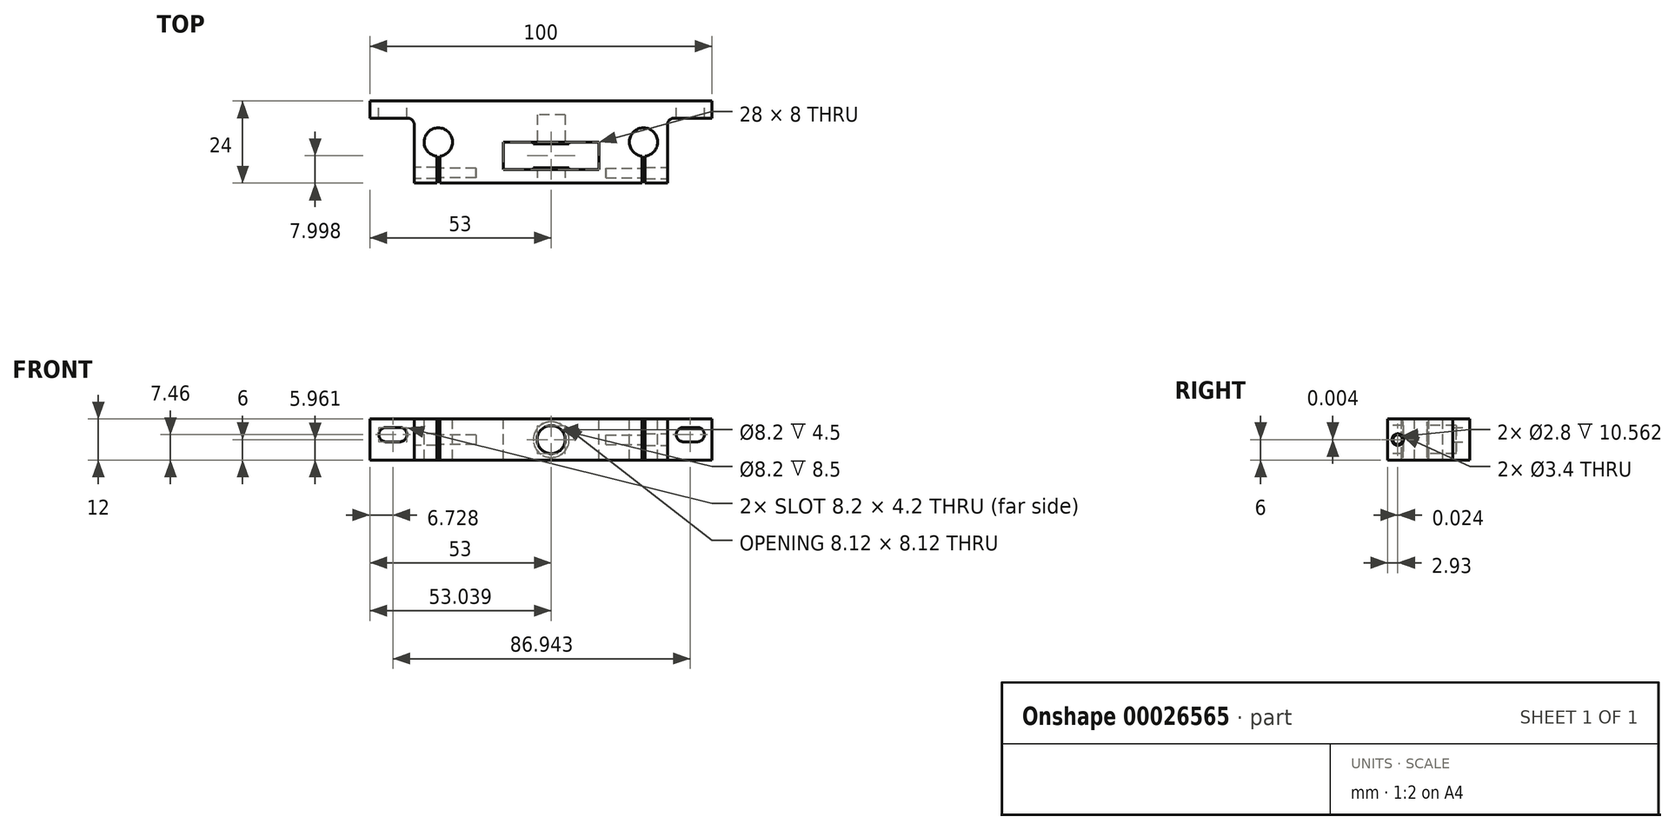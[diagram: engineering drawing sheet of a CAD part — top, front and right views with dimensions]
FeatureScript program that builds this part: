
annotation { "Feature Type Name" : "Feature", "Feature Type Description" : "" }
export const myFeature = defineFeature(function(context is Context, id is Id, definition is map)
    precondition{}
    {
        {
            var Q0;
            Q0=qCreatedBy(makeId("Top.planeOp"),FACE);
            var sketch = newSketch(context, id + "F0", { "sketchPlane" : qUnion([Q0])});
            skLineSegment(sketch, "E0", {"start": v(-46.35, 12.3) * mm, "end": v(53.65, 12.3) * mm});
            skLineSegment(sketch, "E1", {"start": v(53.65, 12.3) * mm, "end": v(53.65, 7.3) * mm});
            skLineSegment(sketch, "E2", {"start": v(53.65, 7.3) * mm, "end": v(40.65, 7.3) * mm});
            skLineSegment(sketch, "E3", {"start": v(40.65, 7.3) * mm, "end": v(40.65, -11.7) * mm});
            skLineSegment(sketch, "E4", {"start": v(40.65, -11.7) * mm, "end": v(-33.35, -11.7) * mm});
            skLineSegment(sketch, "E5", {"start": v(-33.35, -11.7) * mm, "end": v(-33.35, 7.3) * mm});
            skLineSegment(sketch, "E6", {"start": v(-33.35, 7.3) * mm, "end": v(-46.35, 7.3) * mm});
            skLineSegment(sketch, "E7", {"start": v(-46.35, 7.3) * mm, "end": v(-46.35, 12.3) * mm});
            skSolve(sketch);
        }
        {
            var Q0;
            Q0=qSketchRegion(id+"F0",true);
            extrude(context, id + "F1", {"entities" : qUnion([Q0]), "depth" : 12 * mm});
        }
        {
            var Q0;
            Q0=makeQuery(id+"F1.opExtrude","CAP_FACE",FACE,{"disambiguationData":[OSD([sQuery(id+"F0.wireOp",EDGE,"E0"),sQuery(id+"F0.wireOp",EDGE,"E1"),sQuery(id+"F0.wireOp",EDGE,"E2"),sQuery(id+"F0.wireOp",EDGE,"E3"),sQuery(id+"F0.wireOp",EDGE,"E4"),sQuery(id+"F0.wireOp",EDGE,"E5"),sQuery(id+"F0.wireOp",EDGE,"E6"),sQuery(id+"F0.wireOp",EDGE,"E7")])],"isStart":false});
            var sketch = newSketch(context, id + "F2", { "sketchPlane" : qUnion([Q0])});
            skCircle(sketch, "E8", {"center": v(-26.35, 0.3) * mm, "radius": 4.15 * mm});
            skCircle(sketch, "E9", {"center": v(33.65, 0.3) * mm, "radius": 4.15 * mm});
            skPoint(sketch, "E10", {"position": v(3.65, 12.3) * mm});
            skLineSegment(sketch, "E11.bottom", {"start": v(33.21, -3.01) * mm, "end": v(34.09, -3.01) * mm});
            skLineSegment(sketch, "E11.top", {"start": v(33.21, -12.27) * mm, "end": v(34.09, -12.27) * mm});
            skLineSegment(sketch, "E11.left", {"start": v(33.21, -3.01) * mm, "end": v(33.21, -12.27) * mm});
            skLineSegment(sketch, "E11.right", {"start": v(34.09, -3.01) * mm, "end": v(34.09, -12.27) * mm});
            skPoint(sketch, "E12", {"position": v(33.65, -3.01) * mm});
            skLineSegment(sketch, "E13", {"start": v(3.65, 12.3) * mm, "end": v(3.65, -11.7) * mm, "construction": true});
            skLineSegment(sketch, "E14.MirrorCS", {"start": v(-25.91, -12.27) * mm, "end": v(-26.79, -12.27) * mm});
            skLineSegment(sketch, "E15.MirrorCS", {"start": v(-26.79, -3.01) * mm, "end": v(-26.79, -12.27) * mm});
            skLineSegment(sketch, "E16.MirrorCS", {"start": v(-25.91, -3.01) * mm, "end": v(-26.79, -3.01) * mm});
            skLineSegment(sketch, "E17.MirrorCS", {"start": v(-25.91, -3.01) * mm, "end": v(-25.91, -12.27) * mm});
            skSolve(sketch);
        }
        {
            var Q0;
            Q0=qSketchRegion(id+"F2",true);
            var Q1;
            {var subQ3=sQuery(id+"F2.wireOp",EDGE,"E11.bottom");Q1=makeQuery(id+"F2.imprint","IMPRINT",FACE,{"disambiguationData":[TD([[makeQuery(id+"F2.imprint","IMPRINT",EDGE,{"derivedFrom":subQ3}),-1.0]])]});}
            var Q2;
            {var subQ3=sQuery(id+"F2.wireOp",EDGE,"E16.MirrorCS");Q2=makeQuery(id+"F2.imprint","IMPRINT",FACE,{"disambiguationData":[TD([[makeQuery(id+"F2.imprint","IMPRINT",EDGE,{"derivedFrom":subQ3}),1.0]])]});}
            extrude(context, id + "F3", {"entities" : qUnion([Q0, Q1, Q2]), "operationType" : NewBodyOperationType.REMOVE, "endBound" : BoundingType.THROUGH_ALL, "oppositeDirection" : true, "depth" : 25 * mm});
        }
        {
            var Q0;
            Q0=makeQuery(id+"F1.opExtrude","SWEPT_FACE",FACE,{"disambiguationData":[OSD([sQuery(id+"F0.wireOp",EDGE,"E0")])]});
            var sketch = newSketch(context, id + "F4", { "sketchPlane" : qUnion([Q0])});
            skLineSegment(sketch, "E18", {"start": v(-53.65, 7.46) * mm, "end": v(46.35, 7.46) * mm, "construction": true});
            skLineSegment(sketch, "E19.bottom", {"start": v(-49.32, 9.56) * mm, "end": v(-45.32, 9.56) * mm});
            skLineSegment(sketch, "E19.top", {"start": v(-49.32, 5.36) * mm, "end": v(-45.32, 5.36) * mm});
            skArc(sketch, "E20", {"start": v(-45.32, 5.36) * mm, "mid": v(-43.22, 7.46) * mm, "end": v(-45.32, 9.56) * mm});
            skArc(sketch, "E21", {"start": v(-49.32, 9.56) * mm, "mid": v(-51.42, 7.46) * mm, "end": v(-49.32, 5.36) * mm});
            skLineSegment(sketch, "E22.top", {"start": v(37.62, 5.36) * mm, "end": v(41.62, 5.36) * mm});
            skLineSegment(sketch, "E22.bottom", {"start": v(37.62, 9.56) * mm, "end": v(41.62, 9.56) * mm});
            skArc(sketch, "E23", {"start": v(37.62, 9.56) * mm, "mid": v(35.52, 7.46) * mm, "end": v(37.62, 5.36) * mm});
            skArc(sketch, "E24", {"start": v(41.62, 5.36) * mm, "mid": v(43.72, 7.46) * mm, "end": v(41.62, 9.56) * mm});
            skSolve(sketch);
        }
        {
            var Q0;
            Q0=qSketchRegion(id+"F4",true);
            extrude(context, id + "F5", {"entities" : qUnion([Q0]), "operationType" : NewBodyOperationType.REMOVE, "endBound" : BoundingType.THROUGH_ALL, "oppositeDirection" : true, "depth" : 25 * mm});
        }
        {
            var Q0;
            Q0=makeQuery(id+"F1.opExtrude","SWEPT_FACE",FACE,{"disambiguationData":[OSD([sQuery(id+"F0.wireOp",EDGE,"E4")])]});
            var sketch = newSketch(context, id + "F6", { "sketchPlane" : qUnion([Q0])});
            skLineSegment(sketch, "E25", {"start": v(-33.35, 6) * mm, "end": v(40.65, 6) * mm, "construction": true});
            skCircle(sketch, "E26", {"center": v(6.65, 6) * mm, "radius": 4.1 * mm});
            skSolve(sketch);
        }
        {
            var Q0;
            Q0=qSketchRegion(id+"F6",true);
            extrude(context, id + "F7", {"entities" : qUnion([Q0]), "operationType" : NewBodyOperationType.REMOVE, "oppositeDirection" : true, "depth" : 20 * mm});
        }
        {
            var Q0;
            Q0=makeQuery(id+"F1.opExtrude","CAP_FACE",FACE,{"disambiguationData":[OSD([sQuery(id+"F0.wireOp",EDGE,"E0"),sQuery(id+"F0.wireOp",EDGE,"E1"),sQuery(id+"F0.wireOp",EDGE,"E2"),sQuery(id+"F0.wireOp",EDGE,"E3"),sQuery(id+"F0.wireOp",EDGE,"E4"),sQuery(id+"F0.wireOp",EDGE,"E5"),sQuery(id+"F0.wireOp",EDGE,"E6"),sQuery(id+"F0.wireOp",EDGE,"E7")])],"isStart":false});
            var sketch = newSketch(context, id + "F8", { "sketchPlane" : qUnion([Q0])});
            skLineSegment(sketch, "E27.bottom", {"start": v(-7.35, 0.3) * mm, "end": v(20.65, 0.3) * mm});
            skLineSegment(sketch, "E27.top", {"start": v(-7.35, -7.7) * mm, "end": v(20.65, -7.7) * mm});
            skLineSegment(sketch, "E27.left", {"start": v(-7.35, 0.3) * mm, "end": v(-7.35, -7.7) * mm});
            skLineSegment(sketch, "E27.right", {"start": v(20.65, 0.3) * mm, "end": v(20.65, -7.7) * mm});
            skLineSegment(sketch, "E28", {"start": v(6.65, 12.3) * mm, "end": v(6.65, -11.7) * mm, "construction": true});
            skLineSegment(sketch, "E29", {"start": v(6.65, 0.3) * mm, "end": v(6.65, -7.7) * mm});
            skSolve(sketch);
        }
        {
            var Q0;
            Q0=qSketchRegion(id+"F8",true);
            extrude(context, id + "F9", {"entities" : qUnion([Q0]), "operationType" : NewBodyOperationType.REMOVE, "endBound" : BoundingType.THROUGH_ALL, "oppositeDirection" : true, "depth" : 25 * mm});
        }
        {
            var Q0;
            Q0=makeQuery(id+"F9.boolean.opBoolean","COPY",FACE,{"derivedFrom":makeQuery(id+"F9.opExtrude","SWEPT_FACE",FACE,{"disambiguationData":[OSD([sQuery(id+"F8.wireOp",EDGE,"E27.bottom")])]})});
            var sketch = newSketch(context, id + "F10", { "sketchPlane" : qUnion([Q0])});
            skCircle(sketch, "E30", {"center": v(6.65, 6) * mm, "radius": 5.2 * mm});
            skSolve(sketch);
        }
        {
            var Q0;
            Q0=makeQuery(id+"F10.imprint","IMPRINT",FACE,{"disambiguationData":[TD([[makeQuery(id+"F10.imprint","IMPRINT",EDGE,{"derivedFrom":sQuery(id+"F10.wireOp",EDGE,"E30")}),1.0]])]});
            extrude(context, id + "F11", {"entities" : qUnion([Q0]), "operationType" : NewBodyOperationType.ADD, "depth" : 0.5 * mm});
        }
        {
            var Q0;
            Q0=makeQuery(id+"F9.boolean.opBoolean","COPY",FACE,{"derivedFrom":makeQuery(id+"F9.opExtrude","SWEPT_FACE",FACE,{"disambiguationData":[OSD([sQuery(id+"F8.wireOp",EDGE,"E27.top")])]})});
            var sketch = newSketch(context, id + "F12", { "sketchPlane" : qUnion([Q0])});
            skCircle(sketch, "E31", {"center": v(-6.65, 6) * mm, "radius": 5.25 * mm});
            skSolve(sketch);
        }
        {
            var Q0;
            Q0=makeQuery(id+"F12.imprint","IMPRINT",FACE,{"disambiguationData":[TD([[makeQuery(id+"F12.imprint","IMPRINT",EDGE,{"derivedFrom":sQuery(id+"F12.wireOp",EDGE,"E31")}),1.0]])]});
            extrude(context, id + "F13", {"entities" : qUnion([Q0]), "operationType" : NewBodyOperationType.ADD, "depth" : 0.5 * mm});
        }
        {
            var Q0;
            Q0=makeQuery(id+"F1.opExtrude","SWEPT_FACE",FACE,{"disambiguationData":[OSD([sQuery(id+"F0.wireOp",EDGE,"E3")])]});
            var sketch = newSketch(context, id + "F14", { "sketchPlane" : qUnion([Q0])});
            skCircle(sketch, "E32", {"center": v(-8.74, 6) * mm, "radius": 1.7 * mm});
            skCircle(sketch, "E33", {"center": v(-8.74, 6) * mm, "radius": 1.4 * mm});
            skLineSegment(sketch, "E34", {"start": v(-11.7, 6) * mm, "end": v(-3.84, 6) * mm, "construction": true});
            skSolve(sketch);
        }
        {
            var Q0;
            Q0=makeQuery(id+"F14.imprint","IMPRINT",FACE,{"disambiguationData":[TD([[makeQuery(id+"F14.imprint","IMPRINT",EDGE,{"derivedFrom":sQuery(id+"F14.wireOp",EDGE,"E33")}),1.0]])]});
            extrude(context, id + "F15", {"entities" : qUnion([Q0]), "operationType" : NewBodyOperationType.REMOVE, "oppositeDirection" : true, "depth" : 18 * mm});
        }
        {
            var Q0;
            Q0=makeQuery(id+"F14.imprint","IMPRINT",FACE,{"disambiguationData":[TD([[makeQuery(id+"F14.imprint","IMPRINT",EDGE,{"derivedFrom":sQuery(id+"F14.wireOp",EDGE,"E33")}),1.0]])]});
            var Q1;
            Q1=makeQuery(id+"F14.imprint","IMPRINT",FACE,{"disambiguationData":[TD([[makeQuery(id+"F14.imprint","IMPRINT",EDGE,{"derivedFrom":sQuery(id+"F14.wireOp",EDGE,"E32")}),1.0]])]});
            extrude(context, id + "F16", {"entities" : qUnion([Q0, Q1]), "operationType" : NewBodyOperationType.REMOVE, "endBound" : BoundingType.UP_TO_NEXT, "oppositeDirection" : true, "depth" : 7 * mm});
        }
        {
            var Q0;
            Q0=makeQuery(id+"F1.opExtrude","SWEPT_EDGE",EDGE,{"disambiguationData":[OSD([sQuery(id+"F0.wireOp",EDGE,"E2"),sQuery(id+"F0.wireOp",EDGE,"E3")])]});
            fillet(context, id + "F17", {"entities" : qUnion([Q0]), "radius" : 2 * mm, "tangentPropagation" : true, "allowEdgeOverflow" : false});
        }
        {
            var Q0;
            Q0=makeQuery(id+"F1.opExtrude","SWEPT_FACE",FACE,{"disambiguationData":[OSD([sQuery(id+"F0.wireOp",EDGE,"E5")])]});
            var sketch = newSketch(context, id + "F18", { "sketchPlane" : qUnion([Q0])});
            skCircle(sketch, "E35", {"center": v(8.76, 6) * mm, "radius": 1.7 * mm});
            skCircle(sketch, "E36", {"center": v(8.76, 6) * mm, "radius": 1.4 * mm});
            skLineSegment(sketch, "E37", {"start": v(8.76, 0) * mm, "end": v(8.76, 12) * mm, "construction": true});
            skSolve(sketch);
        }
        {
            var Q0;
            Q0=makeQuery(id+"F18.imprint","IMPRINT",FACE,{"disambiguationData":[TD([[makeQuery(id+"F18.imprint","IMPRINT",EDGE,{"derivedFrom":sQuery(id+"F18.wireOp",EDGE,"E36")}),1.0]])]});
            extrude(context, id + "F19", {"entities" : qUnion([Q0]), "operationType" : NewBodyOperationType.REMOVE, "oppositeDirection" : true, "depth" : 18 * mm});
        }
        {
            var Q0;
            Q0=makeQuery(id+"F18.imprint","IMPRINT",FACE,{"disambiguationData":[TD([[makeQuery(id+"F18.imprint","IMPRINT",EDGE,{"derivedFrom":sQuery(id+"F18.wireOp",EDGE,"E36")}),1.0]])]});
            var Q1;
            Q1=makeQuery(id+"F18.imprint","IMPRINT",FACE,{"disambiguationData":[TD([[makeQuery(id+"F18.imprint","IMPRINT",EDGE,{"derivedFrom":sQuery(id+"F18.wireOp",EDGE,"E35")}),1.0]])]});
            extrude(context, id + "F20", {"entities" : qUnion([Q0, Q1]), "operationType" : NewBodyOperationType.REMOVE, "endBound" : BoundingType.UP_TO_NEXT, "oppositeDirection" : true, "depth" : 25 * mm});
        }
        {
            var Q0;
            Q0=makeQuery(id+"F1.opExtrude","SWEPT_EDGE",EDGE,{"disambiguationData":[OSD([sQuery(id+"F0.wireOp",EDGE,"E5"),sQuery(id+"F0.wireOp",EDGE,"E6")])]});
            fillet(context, id + "F21", {"entities" : qUnion([Q0]), "radius" : 2 * mm, "tangentPropagation" : true, "allowEdgeOverflow" : false});
        }
    });
